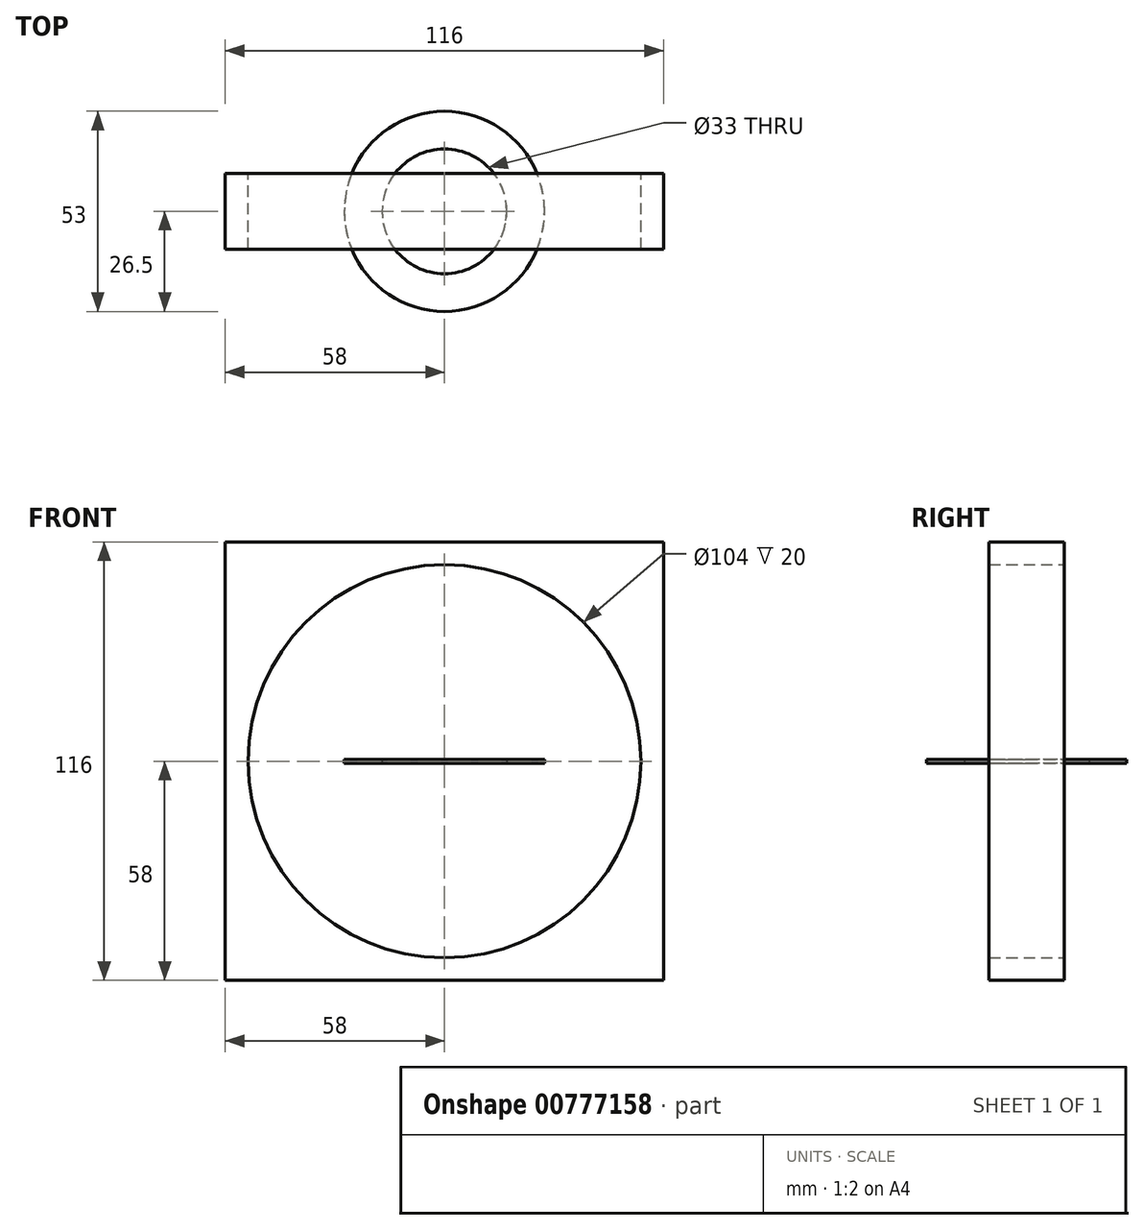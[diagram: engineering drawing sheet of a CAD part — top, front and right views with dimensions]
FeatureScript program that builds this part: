
annotation { "Feature Type Name" : "Feature", "Feature Type Description" : "" }
export const myFeature = defineFeature(function(context is Context, id is Id, definition is map)
    precondition{}
    {
        {
            var Q0;
            Q0=qCreatedBy(makeId("Front.planeOp"),FACE);
            var sketch = newSketch(context, id + "F0", { "sketchPlane" : qUnion([Q0])});
            skCircle(sketch, "E0", {"center": v(0, 0) * mm, "radius": 52 * mm});
            skLineSegment(sketch, "E1", {"start": v(0, 66.87) * mm, "end": v(0, -64.3) * mm, "construction": true});
            skLineSegment(sketch, "E2.bottom", {"start": v(-58, 58) * mm, "end": v(58, 58) * mm});
            skLineSegment(sketch, "E2.top", {"start": v(-58, -58) * mm, "end": v(58, -58) * mm});
            skLineSegment(sketch, "E2.left", {"start": v(-58, 58) * mm, "end": v(-58, -58) * mm});
            skLineSegment(sketch, "E2.right", {"start": v(58, 58) * mm, "end": v(58, -58) * mm});
            skSolve(sketch);
        }
        {
            var Q0;
            Q0=makeQuery(id+"F0.imprint","IMPRINT",FACE,{"disambiguationData":[TD([[makeQuery(id+"F0.imprint","IMPRINT",EDGE,{"derivedFrom":sQuery(id+"F0.wireOp",EDGE,"E0")}),-1.0]])]});
            extrude(context, id + "F1", {"entities" : qUnion([Q0]), "endBound" : BoundingType.SYMMETRIC, "depth" : 20 * mm, "offsetDistance" : 25 * mm});
        }
        {
            var Q0;
            Q0=qCreatedBy(makeId("Top.planeOp"),FACE);
            var sketch = newSketch(context, id + "F2", { "sketchPlane" : qUnion([Q0])});
            skCircle(sketch, "E3", {"center": v(0, 0) * mm, "radius": 26.5 * mm});
            skCircle(sketch, "E4", {"center": v(0, 0) * mm, "radius": 16.5 * mm});
            skSolve(sketch);
        }
        {
            var Q0;
            Q0=makeQuery(id+"F2.imprint","IMPRINT",FACE,{"disambiguationData":[TD([[makeQuery(id+"F2.imprint","IMPRINT",EDGE,{"derivedFrom":sQuery(id+"F2.wireOp",EDGE,"E3")}),1.0]])]});
            extrude(context, id + "F3", {"entities" : qUnion([Q0]), "endBound" : BoundingType.SYMMETRIC, "depth" : 1 * mm, "offsetDistance" : 25 * mm});
        }
    });
